# Revit family: Ray 680D-I LED - Generic
name_source: partatom
category: Lighting Fixtures
revit_build: Autodesk Revit Architecture 2014 (Build: 20140709_2115(x64)
units: mm (PartAtom-declared; Revit-internal decimal feet)

## types (1)
- Ray 680 D/I LED
    Apparent Load = 240 VA
    ArticleNumber = See URL hyperlink
    AssetType = Moveable/Fixed
    BIMObjectName = Ray 680 D/I LED.rfa
    BSAB 96 = SNB.2
    BallastsCELMAEnergyEfficiencyIndex = Class A1/A2
    CCSClassCode = UAC
    CCSClassName = Belysningsarmatur
    CCSTopnode = L
    Colour = Grey
    ControlGearPosition = Integrated
    Description = 70-80-35 General Lighting Systems
    Diameter 1 = 680 mm
    Diameter 2 = 108 mm
    DocumentReference = See URL hyperlink
    Documentation = See URL hyperlink
    Finish = Powder coated
    HasProtectiveEarth = TRUE
    Height 1 = 703 mm
    IP_Code = IP65
    IfcExportAs = IfcLightFixtureType'
    IfcExportType = NOTDEFINED'
    InsulationStandardClass = Class 1 / Class 2
    InternalFuse = Only required in emergency versions
    LampColourRenderingIndex = Ra>80
    LampRating = 28W / 40W
    LampType = LED
    Light Source Definition (family) = Point+Spherical
    Light Source Symbol Size = 610 mm
    LightFixtureMountingType = Pole_top / Wall
    LightFixturePlacingType = Pole / Wall
    LightSource = LED 3000K
    LuminairePowerFactor = >0,9
    LuminaireType = Outdoor Direct/Indirect LED Luminaire
    Manufacturer = Riegens A/S
    ManufacturerURL = www.riegens.com
    Material = Aluminium and PC
    Model = Ray 680 D/I LED
    ModelReference = Ray 680 D/I LED
    NominalVoltage = 220-240V
    Offset from floor = 2900 mm
    OmniClass Number = 23.80.70.00
    OmniClass Title = Lighting
    Optic = Clear front and opal centre diffuser
    PhaseReference = IEC recommendations
    PhotometricPerformance = In accordance with BS EN 13032-1
    ProductInformation = http://riegens.com
    Shape = Circle
    Size = Ø680 mm
    TotalWattage = Max. 28W / 41W
    URL = http://riegens.com
    Uniclass 1.4 = JY73
    Uniclass2 = Pr_70_70_49_43 Light-Emitting Diode (LED) Luminaires
    Version = v.1.0

## geometry (parser evidence)
native form markers: Blend x1, Sweep x7
no freeform markers — native parametric forms only
